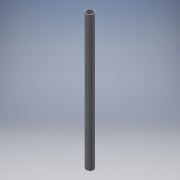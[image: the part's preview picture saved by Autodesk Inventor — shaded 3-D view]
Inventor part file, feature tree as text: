
AUTODESK INVENTOR PART (.ipt)
format: ipt  version: 2017 (Build 210142000, 142)  size: 92,160 bytes
history: native  units: in
note: dims shown in document units (in); Inventor stores cm internally (conversion verified against a paired STEP export)
features: extrude x1, sketch x1
ambient origin geometry x8: Origin, YZ Plane, XZ Plane, XY Plane, X Axis, Y Axis, Z Axis, Center Point
bodies: Solid1 (feature_tree)
feature tree (2):
  extrude  "Extrusion1"  Depth=30.0in
  sketch  "Sketch1"  dims[d0=1.625in d1=1.329in d2=30.0in d3=0.0in]
